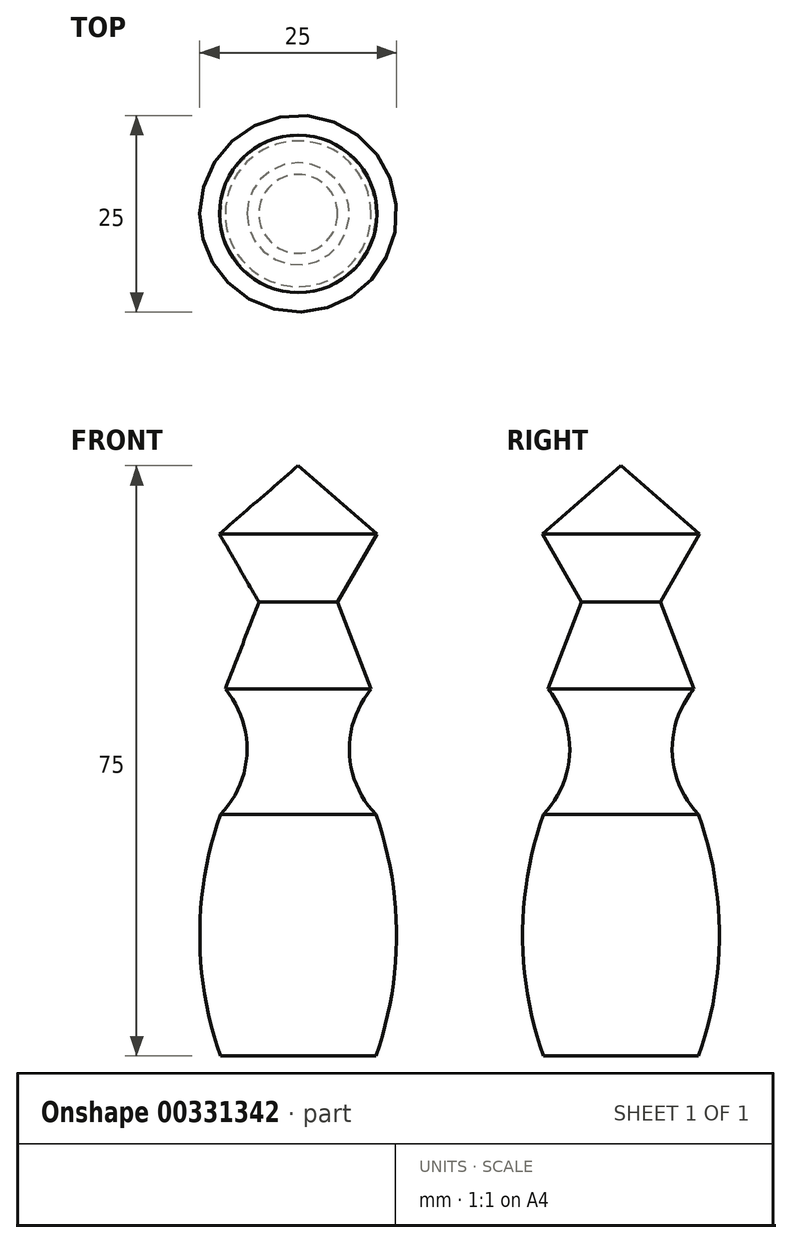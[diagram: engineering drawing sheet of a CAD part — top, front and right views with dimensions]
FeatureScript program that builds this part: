
annotation { "Feature Type Name" : "Feature", "Feature Type Description" : "" }
export const myFeature = defineFeature(function(context is Context, id is Id, definition is map)
    precondition{}
    {
        {
            var Q0;
            Q0=qCreatedBy(makeId("Front.planeOp"),FACE);
            var sketch = newSketch(context, id + "F0", { "sketchPlane" : qUnion([Q0])});
            skArc(sketch, "E0", {"start": v(9.86, -75) * mm, "mid": v(12.5, -59.65) * mm, "end": v(9.86, -44.3) * mm});
            skLineSegment(sketch, "E1", {"start": v(9.86, -75) * mm, "end": v(0, -75) * mm});
            skLineSegment(sketch, "E2", {"start": v(0, -75) * mm, "end": v(0, 0) * mm});
            skLineSegment(sketch, "E3.2", {"start": v(10, -8.66) * mm, "end": v(5, -17.32) * mm});
            skPoint(sketch, "E3.0.midPoint", {"position": v(0, 0) * mm});
            skLineSegment(sketch, "E4", {"start": v(5, -17.32) * mm, "end": v(9.26, -28.39) * mm});
            skArc(sketch, "E5", {"start": v(9.26, -28.39) * mm, "mid": v(6.5, -36.46) * mm, "end": v(9.86, -44.3) * mm});
            skLineSegment(sketch, "E6", {"start": v(10, -8.66) * mm, "end": v(0, 0) * mm});
            skSolve(sketch);
        }
        {
            var Q0;
            Q0=makeQuery(id+"F0.imprint","IMPRINT",FACE,{"disambiguationData":[TD([[makeQuery(id+"F0.imprint","IMPRINT",EDGE,{"derivedFrom":sQuery(id+"F0.wireOp",EDGE,"E0")}),1.0]])]});
            var Q1;
            Q1=sQuery(id+"F0.wireOp",EDGE,"E2");
            revolve(context, id + "F1", {"entities" : qUnion([Q0]), "axis" : qUnion([Q1]), "revolveType" : RevolveType.FULL});
        }
    });
